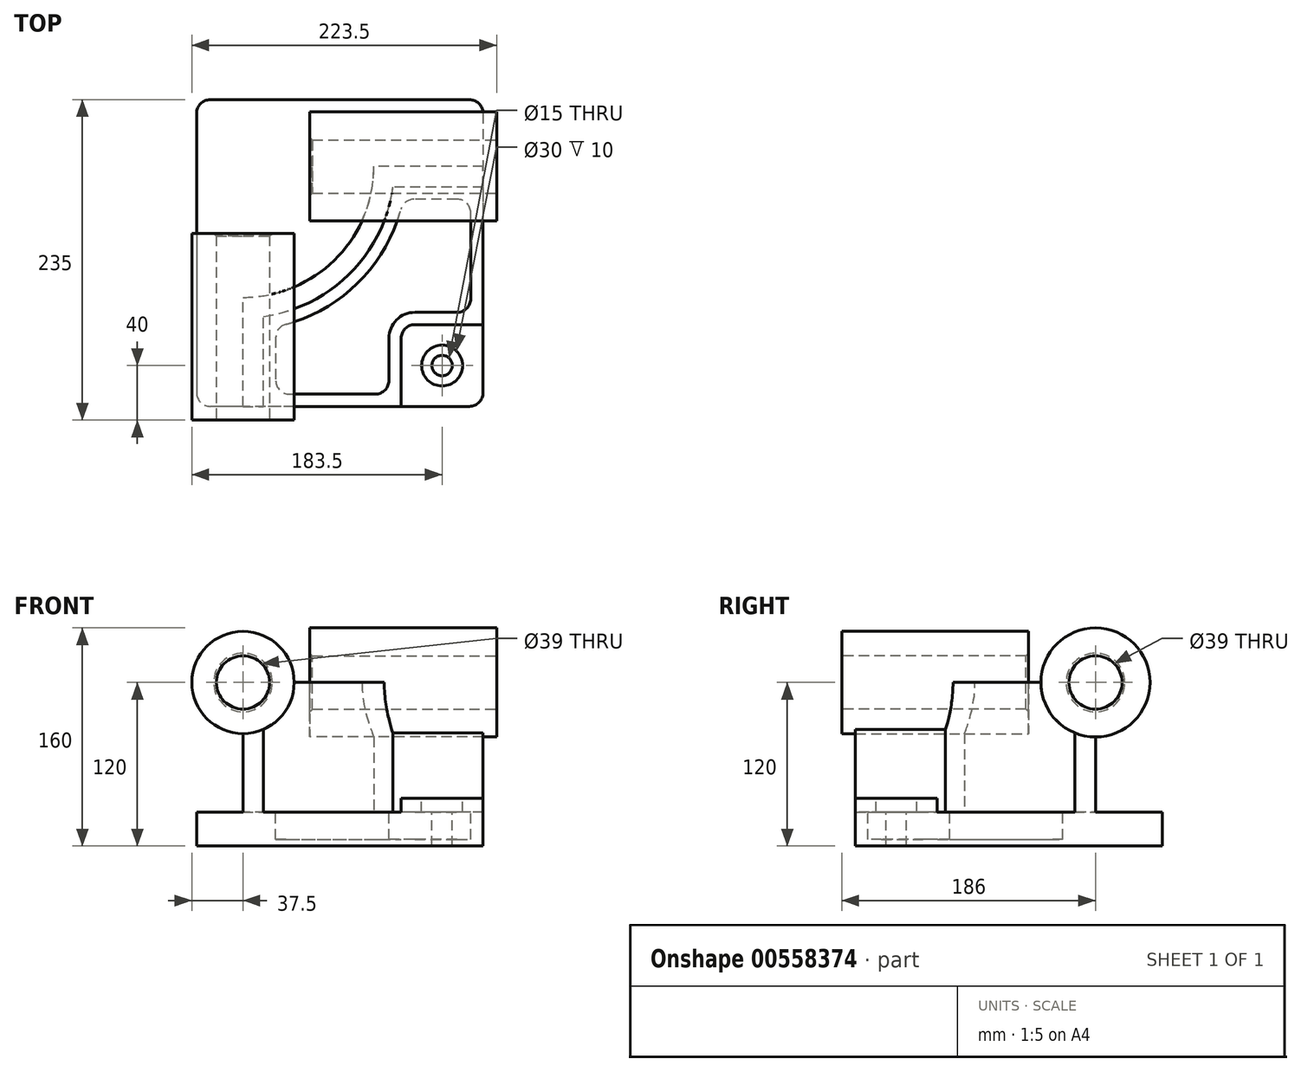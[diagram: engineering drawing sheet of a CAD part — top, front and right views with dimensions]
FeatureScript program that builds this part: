
annotation { "Feature Type Name" : "Feature", "Feature Type Description" : "" }
export const myFeature = defineFeature(function(context is Context, id is Id, definition is map)
    precondition{}
    {
        {
            var Q0;
            Q0=qCreatedBy(makeId("Top.planeOp"),FACE);
            var sketch = newSketch(context, id + "F0", { "sketchPlane" : qUnion([Q0])});
            skLineSegment(sketch, "E0.bottom", {"start": v(105, 112.5) * mm, "end": v(-105, 112.5) * mm});
            skLineSegment(sketch, "E0.top", {"start": v(105, -112.5) * mm, "end": v(-105, -112.5) * mm});
            skLineSegment(sketch, "E0.left", {"start": v(105, 112.5) * mm, "end": v(105, -112.5) * mm});
            skLineSegment(sketch, "E0.right", {"start": v(-105, 112.5) * mm, "end": v(-105, -112.5) * mm});
            skPoint(sketch, "E0.middle", {"position": v(0, 0) * mm});
            skSolve(sketch);
        }
        {
            var Q0;
            Q0=makeQuery(id+"F0.imprint","IMPRINT",FACE,{"disambiguationData":[TD([[makeQuery(id+"F0.imprint","IMPRINT",EDGE,{"derivedFrom":sQuery(id+"F0.wireOp",EDGE,"E0.bottom")}),1.0]])]});
            extrude(context, id + "F1", {"entities" : qUnion([Q0]), "depth" : 25 * mm, "offsetDistance" : 25 * mm});
        }
        {
            var Q0;
            Q0=makeQuery(id+"F1.opExtrude","CAP_FACE",FACE,{"disambiguationData":[OSD([sQuery(id+"F0.wireOp",EDGE,"E0.bottom"),sQuery(id+"F0.wireOp",EDGE,"E0.top"),sQuery(id+"F0.wireOp",EDGE,"E0.left"),sQuery(id+"F0.wireOp",EDGE,"E0.right")])],"isStart":false});
            var sketch = newSketch(context, id + "F2", { "sketchPlane" : qUnion([Q0])});
            skLineSegment(sketch, "E1", {"start": v(-71, -112.5) * mm, "end": v(-71, -32.5) * mm});
            skLineSegment(sketch, "E2", {"start": v(105, 63.5) * mm, "end": v(25, 63.5) * mm});
            skArc(sketch, "E3", {"start": v(-71, -32.5) * mm, "mid": v(-3.12, -4.38) * mm, "end": v(25, 63.5) * mm});
            skLineSegment(sketch, "E4", {"start": v(-71, 63.5) * mm, "end": v(25, 63.5) * mm, "construction": true});
            skLineSegment(sketch, "E5", {"start": v(-71, 63.5) * mm, "end": v(-71, -32.5) * mm, "construction": true});
            skLineSegment(sketch, "E6.0", {"start": v(-56, -112.5) * mm, "end": v(-56, -46.48) * mm});
            skArc(sketch, "E6.1", {"start": v(-56, -46.48) * mm, "mid": v(7.49, -14.99) * mm, "end": v(38.98, 48.5) * mm});
            skLineSegment(sketch, "E6.2", {"start": v(105, 48.5) * mm, "end": v(38.98, 48.5) * mm});
            skLineSegment(sketch, "E7.0", {"start": v(105, 112.5) * mm, "end": v(105, -112.5) * mm});
            skLineSegment(sketch, "E8.0", {"start": v(105, -112.5) * mm, "end": v(-105, -112.5) * mm});
            skLineSegment(sketch, "E9.0.0", {"start": v(-105, -112.5) * mm, "end": v(105, -112.5) * mm});
            skLineSegment(sketch, "E9.0.1", {"start": v(105, -112.5) * mm, "end": v(105, 112.5) * mm});
            skLineSegment(sketch, "E9.0.2", {"start": v(105, 112.5) * mm, "end": v(-105, 112.5) * mm});
            skLineSegment(sketch, "E9.0.3", {"start": v(-105, 112.5) * mm, "end": v(-105, -112.5) * mm});
            skSolve(sketch);
        }
        {
            var Q0;
            {var subQ2=sQuery(id+"F2.wireOp",EDGE,"E1");Q0=makeQuery(id+"F2.imprint","IMPRINT",FACE,{"disambiguationData":[TD([[makeQuery(id+"F2.imprint","IMPRINT",EDGE,{"derivedFrom":subQ2}),-1.0]])]});}
            extrude(context, id + "F3", {"entities" : qUnion([Q0]), "operationType" : NewBodyOperationType.ADD, "depth" : 95 * mm, "offsetDistance" : 25 * mm});
        }
        {
            var Q0;
            Q0=makeQuery(id+"F3.boolean.opBoolean","MERGE",FACE,{"derivedFrom":[makeQuery(id+"F1.opExtrude","SWEPT_FACE",FACE,{"disambiguationData":[OSD([sQuery(id+"F0.wireOp",EDGE,"E0.top")])]}),makeQuery(id+"F3.opExtrude","SWEPT_FACE",FACE,{"disambiguationData":[OSD([sQuery(id+"F2.wireOp",EDGE,"E9.0.0")])]})]});
            var sketch = newSketch(context, id + "F4", { "sketchPlane" : qUnion([Q0])});
            skCircle(sketch, "E10", {"center": v(-71, 120) * mm, "radius": 37.5 * mm});
            skSolve(sketch);
        }
        {
            var Q0;
            Q0 = qSketchRegion(id + "F4", true);
            extrude(context, id + "F5", {"entities" : qUnion([Q0]), "operationType" : NewBodyOperationType.ADD, "depth" : 10 * mm, "offsetDistance" : 25 * mm, "hasSecondDirection" : true, "secondDirectionOppositeDirection" : true, "secondDirectionDepth" : (137 - 10) * mm});
        }
        {
            var Q0;
            Q0=makeQuery(id+"F3.boolean.opBoolean","MERGE",FACE,{"derivedFrom":[makeQuery(id+"F1.opExtrude","SWEPT_FACE",FACE,{"disambiguationData":[OSD([sQuery(id+"F0.wireOp",EDGE,"E0.left")])]}),makeQuery(id+"F3.opExtrude","SWEPT_FACE",FACE,{"disambiguationData":[OSD([sQuery(id+"F2.wireOp",EDGE,"E9.0.1")])]})]});
            var sketch = newSketch(context, id + "F6", { "sketchPlane" : qUnion([Q0])});
            skCircle(sketch, "E11", {"center": v(63.5, 120) * mm, "radius": 40 * mm});
            skSolve(sketch);
        }
        {
            var Q0;
            Q0 = qSketchRegion(id + "F6", true);
            extrude(context, id + "F7", {"entities" : qUnion([Q0]), "operationType" : NewBodyOperationType.ADD, "depth" : 10 * mm, "offsetDistance" : 25 * mm, "hasSecondDirection" : true, "secondDirectionOppositeDirection" : true, "secondDirectionDepth" : 127 * mm});
        }
        {
            var Q0;
            {var subQ0=sQuery(id+"F0.wireOp",EDGE,"E0.left");var subQ1=sQuery(id+"F0.wireOp",EDGE,"E0.top");Q0=makeQuery(id+"F3.boolean.opBoolean","SPLIT",FACE,{"disambiguationData":[TD([makeQuery(id+"F3.opExtrude","SWEPT_FACE",FACE,{"disambiguationData":[OSD([sQuery(id+"F2.wireOp",EDGE,"E6.0")])]})])],"derivedFrom":makeQuery(id+"F1.opExtrude","CAP_FACE",FACE,{"disambiguationData":[OSD([sQuery(id+"F0.wireOp",EDGE,"E0.bottom"),subQ1,subQ0,sQuery(id+"F0.wireOp",EDGE,"E0.right")])],"isStart":false})});}
            var sketch = newSketch(context, id + "F8", { "sketchPlane" : qUnion([Q0])});
            skLineSegment(sketch, "E12.bottom", {"start": v(105, -112.5) * mm, "end": v(45, -112.5) * mm});
            skLineSegment(sketch, "E12.top", {"start": v(105, -52.5) * mm, "end": v(45, -52.5) * mm});
            skLineSegment(sketch, "E12.left", {"start": v(105, -112.5) * mm, "end": v(105, -52.5) * mm});
            skLineSegment(sketch, "E12.right", {"start": v(45, -112.5) * mm, "end": v(45, -52.5) * mm});
            skSolve(sketch);
        }
        {
            var Q0;
            Q0 = qSketchRegion(id + "F8", true);
            extrude(context, id + "F9", {"entities" : qUnion([Q0]), "operationType" : NewBodyOperationType.ADD, "depth" : (35 - 25) * mm, "offsetDistance" : 25 * mm});
        }
        {
            var Q0;
            Q0=makeQuery(id+"F9.opExtrude","SWEPT_EDGE",EDGE,{"disambiguationData":[OSD([sQuery(id+"F8.wireOp",EDGE,"E12.top"),sQuery(id+"F8.wireOp",EDGE,"E12.right")])]});
            fillet(context, id + "F10", {"entities" : qUnion([Q0]), "radius" : 10 * mm, "tangentPropagation" : true, "allowEdgeOverflow" : false});
        }
        {
            var Q0;
            {var subQ0=sQuery(id+"F0.wireOp",EDGE,"E0.left");var subQ1=sQuery(id+"F0.wireOp",EDGE,"E0.top");Q0=makeQuery(id+"F3.boolean.opBoolean","SPLIT",FACE,{"disambiguationData":[TD([makeQuery(id+"F3.opExtrude","SWEPT_FACE",FACE,{"disambiguationData":[OSD([sQuery(id+"F2.wireOp",EDGE,"E6.0")])]})])],"derivedFrom":makeQuery(id+"F1.opExtrude","CAP_FACE",FACE,{"disambiguationData":[OSD([sQuery(id+"F0.wireOp",EDGE,"E0.bottom"),subQ1,subQ0,sQuery(id+"F0.wireOp",EDGE,"E0.right")])],"isStart":false})});}
            var sketch = newSketch(context, id + "F11", { "sketchPlane" : qUnion([Q0])});
            skLineSegment(sketch, "E13.0", {"start": v(-47, -54.08) * mm, "end": v(-47, -103.5) * mm});
            skArc(sketch, "E13.1", {"start": v(46.58, 39.5) * mm, "mid": v(13.85, -21.35) * mm, "end": v(-47, -54.08) * mm});
            skLineSegment(sketch, "E13.2", {"start": v(-47, -103.5) * mm, "end": v(36, -103.5) * mm});
            skLineSegment(sketch, "E13.3", {"start": v(96, 39.5) * mm, "end": v(46.58, 39.5) * mm});
            skLineSegment(sketch, "E13.4", {"start": v(36, -103.5) * mm, "end": v(36, -62.5) * mm});
            skArc(sketch, "E13.5", {"start": v(36, -62.5) * mm, "mid": v(41.56, -49.06) * mm, "end": v(55, -43.5) * mm});
            skLineSegment(sketch, "E13.6", {"start": v(55, -43.5) * mm, "end": v(96, -43.5) * mm});
            skLineSegment(sketch, "E13.7", {"start": v(96, -43.5) * mm, "end": v(96, 39.5) * mm});
            skSolve(sketch);
        }
        {
            var Q0;
            Q0=makeQuery(id+"F11.imprint","IMPRINT",FACE,{"disambiguationData":[TD([[makeQuery(id+"F11.imprint","IMPRINT",EDGE,{"derivedFrom":sQuery(id+"F11.wireOp",EDGE,"E13.0")}),1.0]])]});
            extrude(context, id + "F12", {"entities" : qUnion([Q0]), "operationType" : NewBodyOperationType.REMOVE, "oppositeDirection" : true, "depth" : (25 - 5) * mm, "offsetDistance" : 25 * mm});
        }
        {
            var Q0;
            Q0=makeQuery(id+"F9.opExtrude","CAP_FACE",FACE,{"disambiguationData":[OSD([sQuery(id+"F8.wireOp",EDGE,"E12.bottom"),sQuery(id+"F8.wireOp",EDGE,"E12.top"),sQuery(id+"F8.wireOp",EDGE,"E12.left"),sQuery(id+"F8.wireOp",EDGE,"E12.right")])],"isStart":false});
            var sketch = newSketch(context, id + "F13", { "sketchPlane" : qUnion([Q0])});
            skCircle(sketch, "E14", {"center": v(75, -82.5) * mm, "radius": 15 * mm});
            skSolve(sketch);
        }
        {
            var Q0;
            Q0=sQuery(id+"F13.wireOp",VERTEX,"E14.center");
            var Q1;
            Q1=makeQuery(id+"F1.opExtrude","SWEPT_BODY",BODY,{"disambiguationData":[OSD([sQuery(id+"F0.wireOp",EDGE,"E0.bottom"),sQuery(id+"F0.wireOp",EDGE,"E0.top"),sQuery(id+"F0.wireOp",EDGE,"E0.left"),sQuery(id+"F0.wireOp",EDGE,"E0.right")])]});
            hole(context, id + "F14", {"style" : HoleStyle.C_BORE, "endStyle" : HoleEndStyle.THROUGH, "holeDiameter" : 15 * mm, "cBoreDiameter" : 30 * mm, "cBoreDepth" : 10 * mm, "isTappedThrough" : true, "tappedDepth" : 12 * mm, "tapClearance" : 3, "locations" : qUnion([Q0]), "scope" : qUnion([Q1])});
        }
        {
            var Q0;
            Q0=makeQuery(id+"F12.boolean.opBoolean","COPY",EDGE,{"derivedFrom":makeQuery(id+"F12.opExtrude","SWEPT_EDGE",EDGE,{"disambiguationData":[OSD([sQuery(id+"F11.wireOp",EDGE,"E13.0"),sQuery(id+"F11.wireOp",EDGE,"E13.1")])]})});
            var Q1;
            Q1=makeQuery(id+"F12.boolean.opBoolean","COPY",EDGE,{"derivedFrom":makeQuery(id+"F12.opExtrude","SWEPT_EDGE",EDGE,{"disambiguationData":[OSD([sQuery(id+"F11.wireOp",EDGE,"E13.1"),sQuery(id+"F11.wireOp",EDGE,"E13.3")])]})});
            var Q2;
            Q2=makeQuery(id+"F12.boolean.opBoolean","COPY",EDGE,{"derivedFrom":makeQuery(id+"F12.opExtrude","SWEPT_EDGE",EDGE,{"disambiguationData":[OSD([sQuery(id+"F11.wireOp",EDGE,"E13.3"),sQuery(id+"F11.wireOp",EDGE,"E13.7")])]})});
            var Q3;
            Q3=makeQuery(id+"F12.boolean.opBoolean","COPY",EDGE,{"derivedFrom":makeQuery(id+"F12.opExtrude","SWEPT_EDGE",EDGE,{"disambiguationData":[OSD([sQuery(id+"F11.wireOp",EDGE,"E13.0"),sQuery(id+"F11.wireOp",EDGE,"E13.2")])]})});
            var Q4;
            Q4=makeQuery(id+"F12.boolean.opBoolean","COPY",EDGE,{"derivedFrom":makeQuery(id+"F12.opExtrude","SWEPT_EDGE",EDGE,{"disambiguationData":[OSD([sQuery(id+"F11.wireOp",EDGE,"E13.2"),sQuery(id+"F11.wireOp",EDGE,"E13.4")])]})});
            var Q5;
            Q5=makeQuery(id+"F12.boolean.opBoolean","COPY",EDGE,{"derivedFrom":makeQuery(id+"F12.opExtrude","SWEPT_EDGE",EDGE,{"disambiguationData":[OSD([sQuery(id+"F11.wireOp",EDGE,"E13.6"),sQuery(id+"F11.wireOp",EDGE,"E13.7")])]})});
            fillet(context, id + "F15", {"entities" : qUnion([Q0, Q1, Q2, Q3, Q4, Q5]), "radius" : 10 * mm, "tangentPropagation" : true, "allowEdgeOverflow" : false});
        }
        {
            var Q0;
            Q0=makeQuery(id+"F5.opExtrude","CAP_FACE",FACE,{"disambiguationData":[OSD([sQuery(id+"F4.wireOp",EDGE,"E10")])],"isStart":false});
            var sketch = newSketch(context, id + "F16", { "sketchPlane" : qUnion([Q0])});
            skCircle(sketch, "E15", {"center": v(-71, 120) * mm, "radius": 19.5 * mm});
            skSolve(sketch);
        }
        {
            var Q0;
            Q0 = qSketchRegion(id + "F16", true);
            extrude(context, id + "F17", {"entities" : qUnion([Q0]), "operationType" : NewBodyOperationType.REMOVE, "endBound" : BoundingType.THROUGH_ALL, "oppositeDirection" : true, "depth" : 144 * mm, "offsetDistance" : 25 * mm});
        }
        {
            var Q0;
            Q0=makeQuery(id+"F7.opExtrude","CAP_FACE",FACE,{"disambiguationData":[OSD([sQuery(id+"F6.wireOp",EDGE,"E11")])],"isStart":false});
            var sketch = newSketch(context, id + "F18", { "sketchPlane" : qUnion([Q0])});
            skCircle(sketch, "E16", {"center": v(63.5, 120) * mm, "radius": 19.5 * mm});
            skSolve(sketch);
        }
        {
            var Q0;
            Q0=makeQuery(id+"F18.imprint","IMPRINT",FACE,{"disambiguationData":[TD([[makeQuery(id+"F18.imprint","IMPRINT",EDGE,{"derivedFrom":sQuery(id+"F18.wireOp",EDGE,"E16")}),1.0]])]});
            extrude(context, id + "F19", {"entities" : qUnion([Q0]), "operationType" : NewBodyOperationType.REMOVE, "endBound" : BoundingType.THROUGH_ALL, "oppositeDirection" : true, "depth" : 25 * mm, "offsetDistance" : 25 * mm});
        }
        {
            var Q0;
            Q0=makeQuery(id+"F17.boolean.opBoolean","COPY",EDGE,{"derivedFrom":makeQuery(id+"F17.opExtrude","CAP_EDGE",EDGE,{"disambiguationData":[OSD([sQuery(id+"F16.wireOp",EDGE,"E15")])],"isStart":true})});
            var Q1;
            Q1=makeQuery(id+"F19.boolean.opBoolean","COPY",EDGE,{"derivedFrom":makeQuery(id+"F19.opExtrude","CAP_EDGE",EDGE,{"disambiguationData":[OSD([sQuery(id+"F18.wireOp",EDGE,"E16")])],"isStart":true})});
            var Q2;
            Q2=makeQuery(id+"F19.boolean.opBoolean","INTERSECT",EDGE,{"derivedFrom":[makeQuery(id+"F7.opExtrude","CAP_FACE",FACE,{"disambiguationData":[OSD([sQuery(id+"F6.wireOp",EDGE,"E11")])],"isStart":true}),makeQuery(id+"F19.opExtrude","SWEPT_FACE",FACE,{"disambiguationData":[OSD([sQuery(id+"F18.wireOp",EDGE,"E16")])]})]});
            var Q3;
            Q3=makeQuery(id+"F17.boolean.opBoolean","INTERSECT",EDGE,{"derivedFrom":[makeQuery(id+"F5.opExtrude","CAP_FACE",FACE,{"disambiguationData":[OSD([sQuery(id+"F4.wireOp",EDGE,"E10")])],"isStart":true}),makeQuery(id+"F17.opExtrude","SWEPT_FACE",FACE,{"disambiguationData":[OSD([sQuery(id+"F16.wireOp",EDGE,"E15")])]})]});
            chamfer(context, id + "F20", {"entities" : qUnion([Q0, Q1, Q2, Q3]), "width" : 2 * mm, "tangentPropagation" : true});
        }
        {
            var Q0;
            Q0=makeQuery(id+"F9.boolean.opBoolean","MERGE",EDGE,{"derivedFrom":[makeQuery(id+"F1.opExtrude","SWEPT_EDGE",EDGE,{"disambiguationData":[OSD([sQuery(id+"F0.wireOp",EDGE,"E0.top"),sQuery(id+"F0.wireOp",EDGE,"E0.left")])]}),makeQuery(id+"F9.opExtrude","SWEPT_EDGE",EDGE,{"disambiguationData":[OSD([sQuery(id+"F8.wireOp",EDGE,"E12.bottom"),sQuery(id+"F8.wireOp",EDGE,"E12.left")])]})]});
            var Q1;
            Q1=makeQuery(id+"F1.opExtrude","SWEPT_EDGE",EDGE,{"disambiguationData":[OSD([sQuery(id+"F0.wireOp",EDGE,"E0.bottom"),sQuery(id+"F0.wireOp",EDGE,"E0.left")])]});
            var Q2;
            Q2=makeQuery(id+"F1.opExtrude","SWEPT_EDGE",EDGE,{"disambiguationData":[OSD([sQuery(id+"F0.wireOp",EDGE,"E0.top"),sQuery(id+"F0.wireOp",EDGE,"E0.right")])]});
            var Q3;
            Q3=makeQuery(id+"F1.opExtrude","SWEPT_EDGE",EDGE,{"disambiguationData":[OSD([sQuery(id+"F0.wireOp",EDGE,"E0.bottom"),sQuery(id+"F0.wireOp",EDGE,"E0.right")])]});
            fillet(context, id + "F21", {"entities" : qUnion([Q0, Q1, Q2, Q3]), "radius" : 10 * mm, "tangentPropagation" : true, "allowEdgeOverflow" : false});
        }
    });
